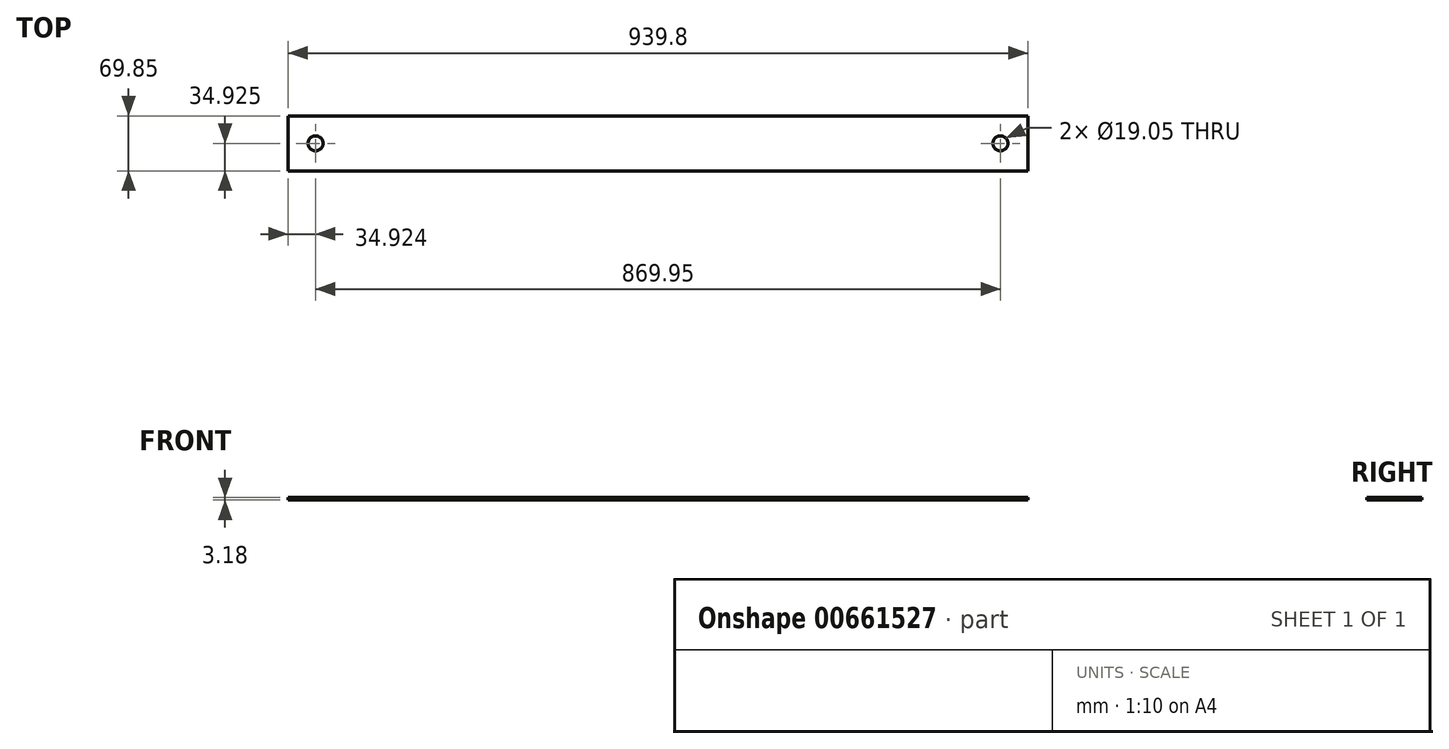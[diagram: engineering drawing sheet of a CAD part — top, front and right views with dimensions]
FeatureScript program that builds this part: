
annotation { "Feature Type Name" : "Feature", "Feature Type Description" : "" }
export const myFeature = defineFeature(function(context is Context, id is Id, definition is map)
    precondition{}
    {
        {
            var Q0;
            Q0=qCreatedBy(makeId("Top.planeOp"),FACE);
            var sketch = newSketch(context, id + "F0", { "sketchPlane" : qUnion([Q0])});
            skLineSegment(sketch, "E0.bottom", {"start": v(-467.15, -74.01) * mm, "end": v(472.65, -74.01) * mm});
            skLineSegment(sketch, "E0.top", {"start": v(-467.15, -143.86) * mm, "end": v(472.65, -143.86) * mm});
            skLineSegment(sketch, "E0.left", {"start": v(-467.15, -74.01) * mm, "end": v(-467.15, -143.86) * mm});
            skLineSegment(sketch, "E0.right", {"start": v(472.65, -74.01) * mm, "end": v(472.65, -143.86) * mm});
            skSolve(sketch);
        }
        {
            var Q0;
            Q0 = qSketchRegion(id + "F0", true);
            extrude(context, id + "F1", {"entities" : qUnion([Q0]), "depth" : 3.17 * mm, "offsetDistance" : 25.4 * mm});
        }
        {
            var Q0;
            Q0=makeQuery(id+"F1.opExtrude","CAP_FACE",FACE,{"disambiguationData":[OSD([sQuery(id+"F0.wireOp",EDGE,"E0.bottom"),sQuery(id+"F0.wireOp",EDGE,"E0.top"),sQuery(id+"F0.wireOp",EDGE,"E0.left"),sQuery(id+"F0.wireOp",EDGE,"E0.right")])],"isStart":false});
            var sketch = newSketch(context, id + "F2", { "sketchPlane" : qUnion([Q0])});
            skCircle(sketch, "E1", {"center": v(-432.23, -108.94) * mm, "radius": 9.53 * mm});
            skCircle(sketch, "E2", {"center": v(437.72, -108.94) * mm, "radius": 9.52 * mm});
            skPoint(sketch, "E2.centerSnap0", {"position": v(472.65, -108.94) * mm});
            skSolve(sketch);
        }
        {
            var Q0;
            Q0 = qSketchRegion(id + "F2", true);
            extrude(context, id + "F3", {"entities" : qUnion([Q0]), "operationType" : NewBodyOperationType.REMOVE, "endBound" : BoundingType.THROUGH_ALL, "oppositeDirection" : true, "depth" : 25.4 * mm, "offsetDistance" : 25.4 * mm});
        }
    });
